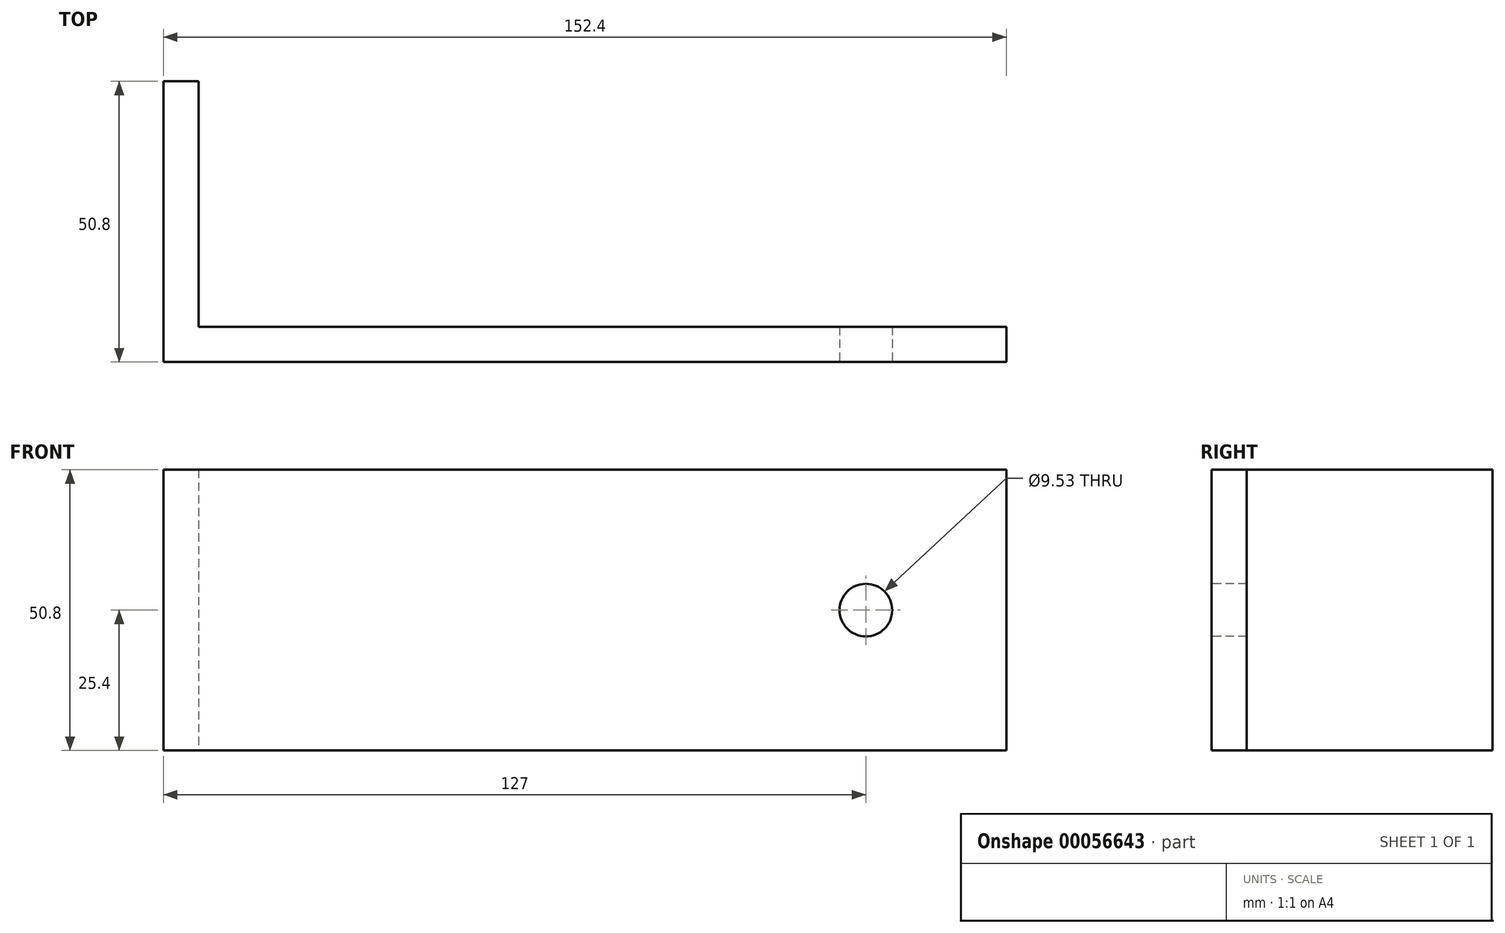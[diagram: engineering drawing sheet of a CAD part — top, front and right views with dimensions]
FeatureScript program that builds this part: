
annotation { "Feature Type Name" : "Feature", "Feature Type Description" : "" }
export const myFeature = defineFeature(function(context is Context, id is Id, definition is map)
    precondition{}
    {
        {
            var Q0;
            Q0=qCreatedBy(makeId("Top.planeOp"),FACE);
            var sketch = newSketch(context, id + "F0", { "sketchPlane" : qUnion([Q0])});
            skLineSegment(sketch, "E0", {"start": v(0, 233.46) * mm, "end": v(-222.25, 233.46) * mm});
            skLineSegment(sketch, "E1", {"start": v(-222.25, 233.46) * mm, "end": v(-222.25, 277.91) * mm});
            skLineSegment(sketch, "E2", {"start": v(-222.25, 277.91) * mm, "end": v(-228.6, 277.91) * mm});
            skLineSegment(sketch, "E3", {"start": v(-228.6, 277.91) * mm, "end": v(-228.6, 227.11) * mm});
            skLineSegment(sketch, "E4", {"start": v(-76.2, 227.11) * mm, "end": v(-228.6, 227.11) * mm});
            skLineSegment(sketch, "E5", {"start": v(-76.2, 227.11) * mm, "end": v(-76.2, 233.46) * mm});
            skSolve(sketch);
        }
        {
            var Q0;
            Q0=qSketchRegion(id+"F0",true);
            extrude(context, id + "F1", {"entities" : qUnion([Q0]), "endBound" : BoundingType.SYMMETRIC, "depth" : 50.8 * mm});
        }
        {
            var Q0;
            Q0=makeQuery(id+"F1.opExtrude","SWEPT_FACE",FACE,{"disambiguationData":[OSD([sQuery(id+"F0.wireOp",EDGE,"E4")])]});
            var sketch = newSketch(context, id + "F2", { "sketchPlane" : qUnion([Q0])});
            skCircle(sketch, "E6", {"center": v(-101.6, 0) * mm, "radius": 4.76 * mm});
            skSolve(sketch);
        }
        {
            var Q0;
            Q0=qSketchRegion(id+"F2",true);
            extrude(context, id + "F3", {"entities" : qUnion([Q0]), "operationType" : NewBodyOperationType.REMOVE, "endBound" : BoundingType.THROUGH_ALL, "oppositeDirection" : true, "depth" : 25.4 * mm});
        }
    });
